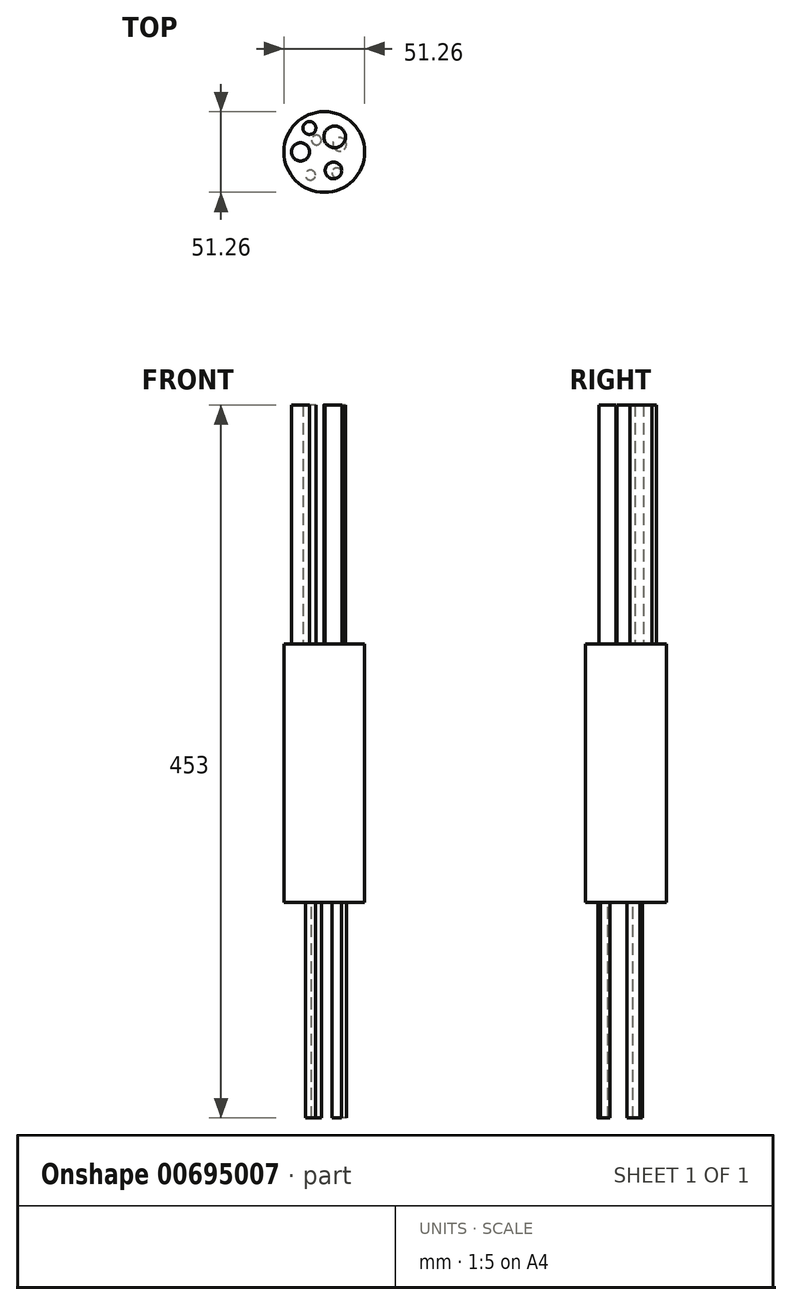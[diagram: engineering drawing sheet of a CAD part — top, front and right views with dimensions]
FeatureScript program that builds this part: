
annotation { "Feature Type Name" : "Feature", "Feature Type Description" : "" }
export const myFeature = defineFeature(function(context is Context, id is Id, definition is map)
    precondition{}
    {
        {
            var Q0;
            Q0=qCreatedBy(makeId("Top.planeOp"),FACE);
            var sketch = newSketch(context, id + "F0", { "sketchPlane" : qUnion([Q0])});
            skCircle(sketch, "E0", {"center": v(0, 0) * mm, "radius": 25.63 * mm});
            skSolve(sketch);
        }
        {
            var Q0;
            Q0 = qSketchRegion(id + "F0", true);
            extrude(context, id + "F1", {"entities" : qUnion([Q0]), "depth" : 164 * mm, "offsetDistance" : 25 * mm});
        }
        {
            var Q0;
            Q0=makeQuery(id+"F1.opExtrude","CAP_FACE",FACE,{"disambiguationData":[OSD([sQuery(id+"F0.wireOp",EDGE,"E0")])],"isStart":true});
            var sketch = newSketch(context, id + "F2", { "sketchPlane" : qUnion([Q0])});
            skCircle(sketch, "E1", {"center": v(-8.85, 14.7) * mm, "radius": 3.19 * mm});
            skCircle(sketch, "E2", {"center": v(7.95, 13.2) * mm, "radius": 3.06 * mm});
            skCircle(sketch, "E3", {"center": v(9.75, -4.8) * mm, "radius": 4.26 * mm});
            skCircle(sketch, "E4", {"center": v(-4.95, -7.5) * mm, "radius": 3.08 * mm});
            skSolve(sketch);
        }
        {
            var Q0;
            Q0 = qSketchRegion(id + "F2", true);
            extrude(context, id + "F3", {"entities" : qUnion([Q0]), "operationType" : NewBodyOperationType.ADD, "depth" : 137 * mm, "offsetDistance" : 25 * mm});
        }
        {
            var Q0;
            Q0=makeQuery(id+"F1.opExtrude","CAP_FACE",FACE,{"disambiguationData":[OSD([sQuery(id+"F0.wireOp",EDGE,"E0")])],"isStart":false});
            var sketch = newSketch(context, id + "F4", { "sketchPlane" : qUnion([Q0])});
            skCircle(sketch, "E5", {"center": v(-9.45, 15.18) * mm, "radius": 4.1 * mm});
            skCircle(sketch, "E6", {"center": v(6.63, 9.54) * mm, "radius": 6.87 * mm});
            skCircle(sketch, "E7", {"center": v(5.83, -11.77) * mm, "radius": 5.29 * mm});
            skCircle(sketch, "E8", {"center": v(-15.09, 0) * mm, "radius": 5.79 * mm});
            skSolve(sketch);
        }
        {
            var Q0;
            Q0 = qSketchRegion(id + "F4", true);
            extrude(context, id + "F5", {"entities" : qUnion([Q0]), "operationType" : NewBodyOperationType.ADD, "depth" : 152 * mm, "offsetDistance" : 25 * mm});
        }
    });
